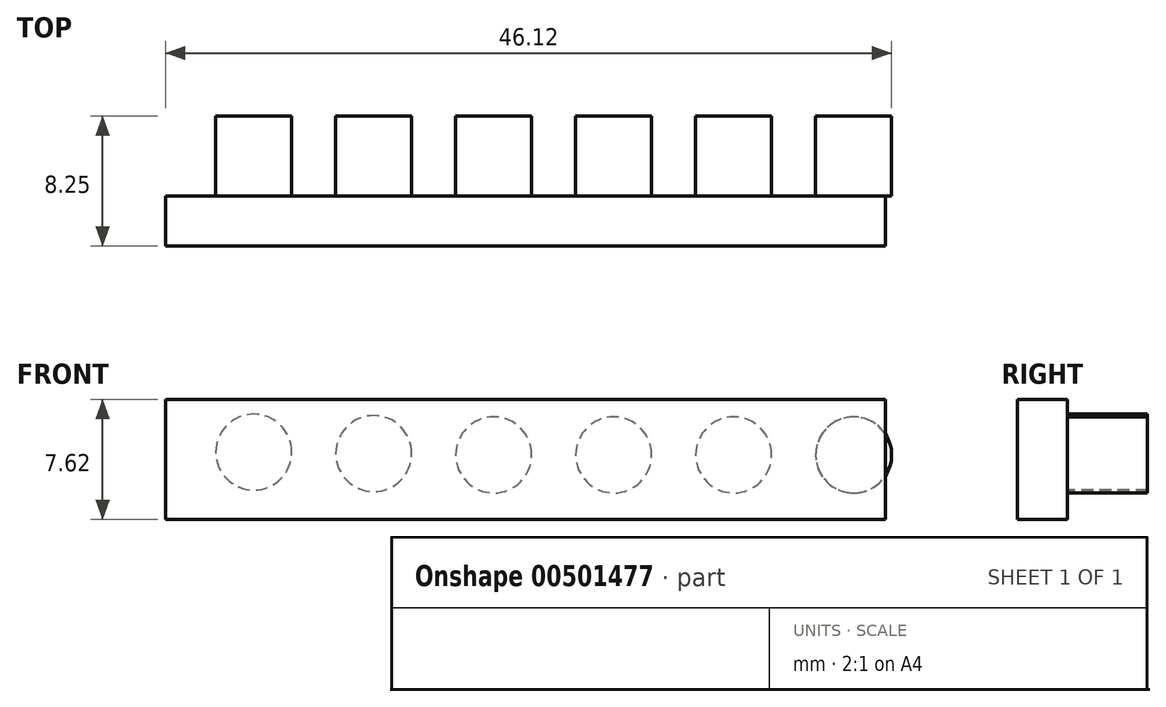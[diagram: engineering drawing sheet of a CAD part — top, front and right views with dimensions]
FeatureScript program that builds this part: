
annotation { "Feature Type Name" : "Feature", "Feature Type Description" : "" }
export const myFeature = defineFeature(function(context is Context, id is Id, definition is map)
    precondition{}
    {
        {
            var Q0;
            Q0=qCreatedBy(makeId("Front.planeOp"),FACE);
            var sketch = newSketch(context, id + "F0", { "sketchPlane" : qUnion([Q0])});
            skLineSegment(sketch, "E0", {"start": v(0, 0) * mm, "end": v(45.72, 0) * mm});
            skLineSegment(sketch, "E1", {"start": v(45.72, 0) * mm, "end": v(45.72, 7.62) * mm});
            skLineSegment(sketch, "E2", {"start": v(45.72, 7.62) * mm, "end": v(0, 7.62) * mm});
            skLineSegment(sketch, "E3", {"start": v(0, 7.62) * mm, "end": v(0, 0) * mm});
            skSolve(sketch);
        }
        {
            var Q0;
            Q0=makeQuery(id+"F0.imprint","IMPRINT",FACE,{"disambiguationData":[TD([[makeQuery(id+"F0.imprint","IMPRINT",EDGE,{"derivedFrom":sQuery(id+"F0.wireOp",EDGE,"E0")}),1.0]])]});
            extrude(context, id + "F1", {"entities" : qUnion([Q0]), "depth" : 3.17 * mm});
        }
        {
            var Q0;
            Q0=qCreatedBy(makeId("Front.planeOp"),FACE);
            var sketch = newSketch(context, id + "F2", { "sketchPlane" : qUnion([Q0])});
            skCircle(sketch, "E4", {"center": v(5.6, 4.27) * mm, "radius": 2.41 * mm});
            skCircle(sketch, "E5.1.0.0", {"center": v(13.23, 4.18) * mm, "radius": 2.41 * mm});
            skCircle(sketch, "E5.2.0.0", {"center": v(20.84, 4.1) * mm, "radius": 2.41 * mm});
            skCircle(sketch, "E6.1.0.0", {"center": v(28.46, 4.1) * mm, "radius": 2.41 * mm});
            skCircle(sketch, "E7.1.0.0", {"center": v(36.08, 4.1) * mm, "radius": 2.41 * mm});
            skCircle(sketch, "E7.2.0.0", {"center": v(43.7, 4.1) * mm, "radius": 2.41 * mm});
            skSolve(sketch);
        }
        {
            var Q0;
            Q0 = qSketchRegion(id + "F2", true);
            extrude(context, id + "F3", {"entities" : qUnion([Q0]), "operationType" : NewBodyOperationType.ADD, "oppositeDirection" : true, "depth" : 5.08 * mm});
        }
    });
